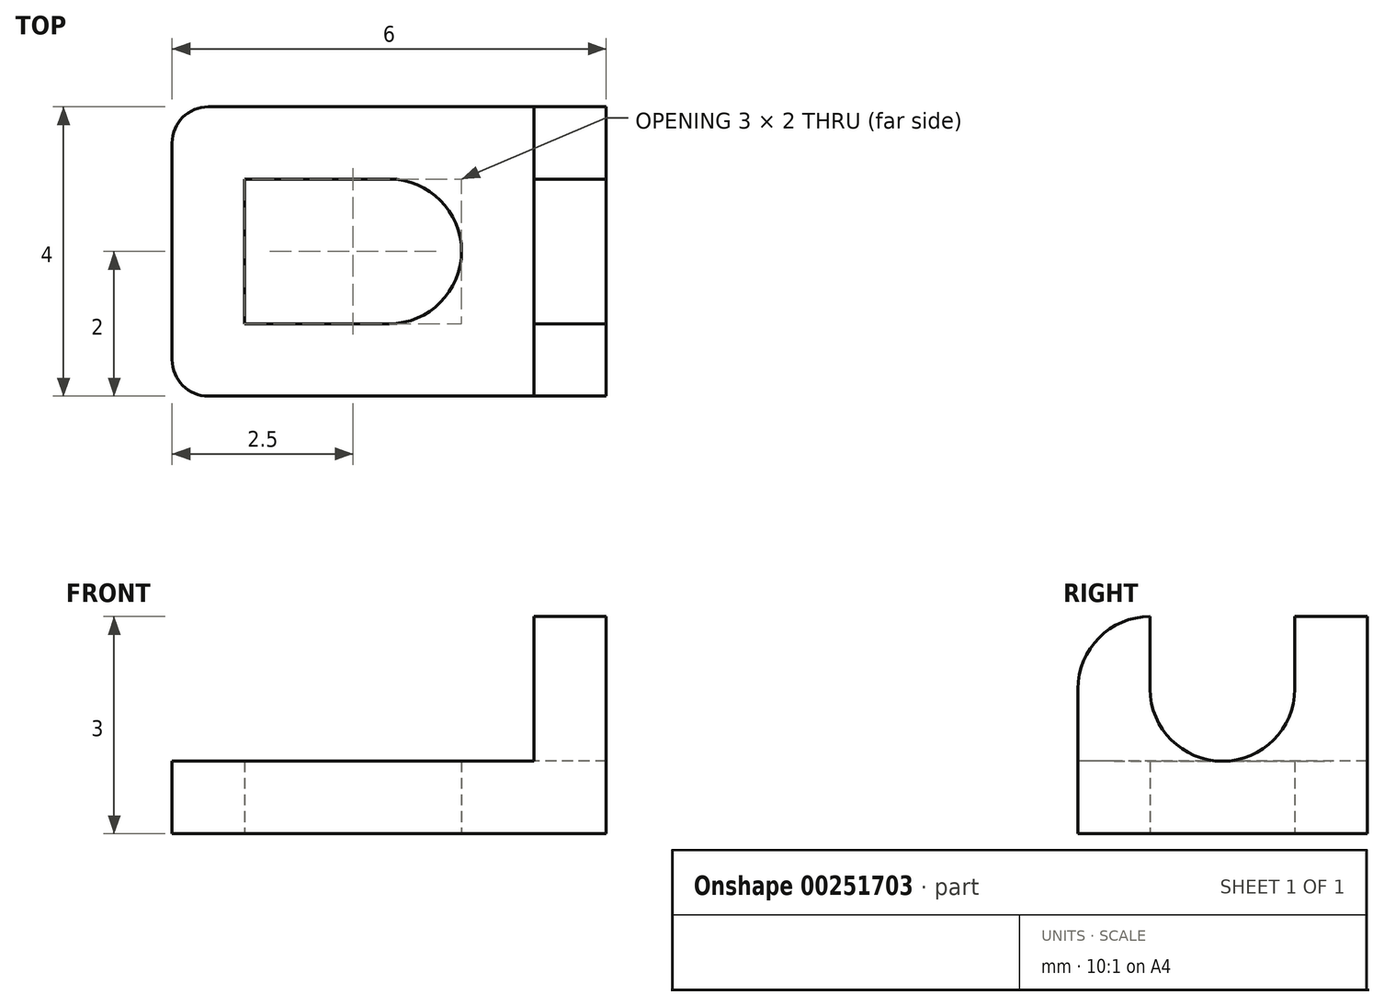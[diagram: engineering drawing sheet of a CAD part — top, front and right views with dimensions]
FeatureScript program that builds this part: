
annotation { "Feature Type Name" : "Feature", "Feature Type Description" : "" }
export const myFeature = defineFeature(function(context is Context, id is Id, definition is map)
    precondition{}
    {
        {
            var Q0;
            Q0=qCreatedBy(makeId("Top.planeOp"),FACE);
            var sketch = newSketch(context, id + "F0", { "sketchPlane" : qUnion([Q0])});
            skLineSegment(sketch, "E0.bottom", {"start": v(0, 0) * mm, "end": v(6, 0) * mm});
            skLineSegment(sketch, "E0.top", {"start": v(0, 4) * mm, "end": v(6, 4) * mm});
            skLineSegment(sketch, "E0.left", {"start": v(0, 0) * mm, "end": v(0, 4) * mm});
            skLineSegment(sketch, "E0.right", {"start": v(6, 0) * mm, "end": v(6, 4) * mm});
            skLineSegment(sketch, "E1", {"start": v(0, 0) * mm, "end": v(0, 1) * mm, "construction": true});
            skLineSegment(sketch, "E2", {"start": v(0, 1) * mm, "end": v(1, 1) * mm, "construction": true});
            skLineSegment(sketch, "E3", {"start": v(1, 1) * mm, "end": v(1, 3) * mm});
            skLineSegment(sketch, "E4", {"start": v(1, 3) * mm, "end": v(3, 3) * mm});
            skLineSegment(sketch, "E5", {"start": v(1, 1) * mm, "end": v(3, 1) * mm});
            skLineSegment(sketch, "E6", {"start": v(3, 1) * mm, "end": v(3, 2) * mm, "construction": true});
            skArc(sketch, "E7", {"start": v(3, 1) * mm, "mid": v(4, 2) * mm, "end": v(3, 3) * mm});
            skSolve(sketch);
        }
        {
            var Q0;
            Q0 = qSketchRegion(id + "F0", true);
            extrude(context, id + "F1", {"entities" : qUnion([Q0]), "depth" : 1 * mm});
        }
        {
            var Q0;
            Q0=makeQuery(id+"F1.opExtrude","SWEPT_EDGE",EDGE,{"disambiguationData":[OSD([sQuery(id+"F0.wireOp",EDGE,"E0.bottom"),sQuery(id+"F0.wireOp",EDGE,"E0.left")])]});
            var Q1;
            Q1=makeQuery(id+"F1.opExtrude","SWEPT_EDGE",EDGE,{"disambiguationData":[OSD([sQuery(id+"F0.wireOp",EDGE,"E0.top"),sQuery(id+"F0.wireOp",EDGE,"E0.left")])]});
            fillet(context, id + "F2", {"entities" : qUnion([Q0, Q1]), "radius" : .5 * mm, "tangentPropagation" : true, "allowEdgeOverflow" : false});
        }
        {
            var Q0;
            Q0=makeQuery(id+"F1.opExtrude","CAP_FACE",FACE,{"disambiguationData":[OSD([sQuery(id+"F0.wireOp",EDGE,"E0.bottom"),sQuery(id+"F0.wireOp",EDGE,"E0.top"),sQuery(id+"F0.wireOp",EDGE,"E0.left"),sQuery(id+"F0.wireOp",EDGE,"E0.right"),sQuery(id+"F0.wireOp",EDGE,"E3"),sQuery(id+"F0.wireOp",EDGE,"E4"),sQuery(id+"F0.wireOp",EDGE,"E5"),sQuery(id+"F0.wireOp",EDGE,"E7")])],"isStart":false});
            var sketch = newSketch(context, id + "F3", { "sketchPlane" : qUnion([Q0])});
            skLineSegment(sketch, "E8", {"start": v(6, 4) * mm, "end": v(5, 4) * mm, "construction": true});
            skLineSegment(sketch, "E9", {"start": v(5, 4) * mm, "end": v(5, 0) * mm});
            skSolve(sketch);
        }
        {
            var Q0;
            {var subQ0=sQuery(id+"F3.wireOp",EDGE,"E9");Q0=makeQuery(id+"F3.imprint","IMPRINT",FACE,{"disambiguationData":[TD([[makeQuery(id+"F3.imprint","IMPRINT",EDGE,{"derivedFrom":subQ0}),1.0]])]});}
            extrude(context, id + "F4", {"entities" : qUnion([Q0]), "operationType" : NewBodyOperationType.ADD, "depth" : 2 * mm});
        }
        {
            var Q0;
            Q0=makeQuery(id+"F4.opExtrude","CAP_EDGE",EDGE,{"disambiguationData":[OSD([sQuery(id+"F0.wireOp",EDGE,"E0.bottom")])],"isStart":false});
            fillet(context, id + "F5", {"entities" : qUnion([Q0]), "radius" : 1 * mm, "tangentPropagation" : true, "allowEdgeOverflow" : false});
        }
        {
            var Q0;
            Q0=makeQuery(id+"F4.opExtrude","SWEPT_FACE",FACE,{"disambiguationData":[OSD([sQuery(id+"F3.wireOp",EDGE,"E9")])]});
            var sketch = newSketch(context, id + "F6", { "sketchPlane" : qUnion([Q0])});
            skLineSegment(sketch, "E10", {"start": v(-4, 3) * mm, "end": v(-3, 3) * mm, "construction": true});
            skLineSegment(sketch, "E11", {"start": v(-3, 3) * mm, "end": v(-3, 2) * mm});
            skLineSegment(sketch, "E12", {"start": v(-3, 2) * mm, "end": v(-2, 2) * mm, "construction": true});
            skLineSegment(sketch, "E13", {"start": v(-2, 2) * mm, "end": v(-1, 2) * mm, "construction": true});
            skLineSegment(sketch, "E14", {"start": v(-1, 2) * mm, "end": v(-1, 3) * mm});
            skArc(sketch, "E15", {"start": v(-3, 2) * mm, "mid": v(-2, 1) * mm, "end": v(-1, 2) * mm});
            skSolve(sketch);
        }
        {
            var Q0;
            {var subQ5=sQuery(id+"F6.wireOp",EDGE,"E11");Q0=makeQuery(id+"F6.imprint","IMPRINT",FACE,{"disambiguationData":[TD([[makeQuery(id+"F6.imprint","IMPRINT",EDGE,{"derivedFrom":subQ5}),1.0]])]});}
            extrude(context, id + "F7", {"entities" : qUnion([Q0]), "operationType" : NewBodyOperationType.REMOVE, "oppositeDirection" : true, "depth" : 25 * mm});
        }
    });
